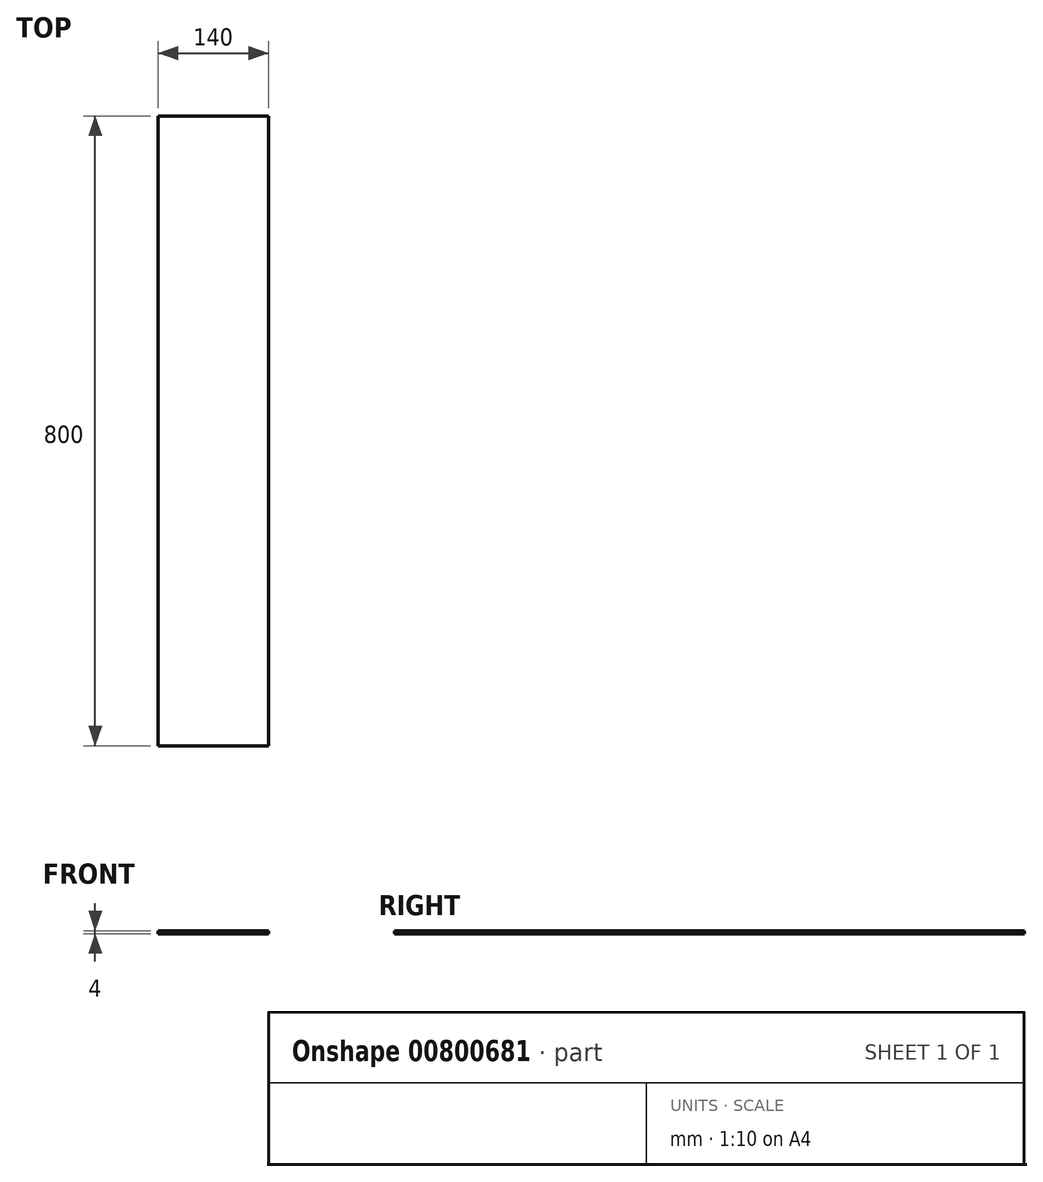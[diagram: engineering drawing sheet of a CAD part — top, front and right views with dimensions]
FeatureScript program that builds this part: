
annotation { "Feature Type Name" : "Feature", "Feature Type Description" : "" }
export const myFeature = defineFeature(function(context is Context, id is Id, definition is map)
    precondition{}
    {
        {
            var Q0;
            Q0=qCreatedBy(makeId("Top.planeOp"),FACE);
            var sketch = newSketch(context, id + "F0", { "sketchPlane" : qUnion([Q0])});
            skLineSegment(sketch, "E0.bottom", {"start": v(70, 400) * mm, "end": v(-70, 400) * mm});
            skLineSegment(sketch, "E0.top", {"start": v(70, -400) * mm, "end": v(-70, -400) * mm});
            skLineSegment(sketch, "E0.left", {"start": v(70, 400) * mm, "end": v(70, -400) * mm});
            skLineSegment(sketch, "E0.right", {"start": v(-70, 400) * mm, "end": v(-70, -400) * mm});
            skPoint(sketch, "E0.middle", {"position": v(0, 0) * mm});
            skSolve(sketch);
        }
        {
            var Q0;
            Q0 = qSketchRegion(id + "F0", true);
            extrude(context, id + "F1", {"entities" : qUnion([Q0]), "depth" : 4 * mm, "offsetDistance" : 25 * mm});
        }
    });
